# Revit family: 210_CAD O Integral ER 19 VLEXG
name_source: partatom
category: Mechanical Equipment
units: mm (PartAtom-declared; Revit-internal decimal feet)

## family parameters
Always vertical = Yes
Cut with Voids When Loaded = No
Part Type = Breaks Into
Room Calculation Point = No
Round Connector Dimension = Use Diameter
Shared = No
Work Plane-Based = No

## types (1)
- CAD O Integral ER 19 VLEXG
    AA1 = 730 mm
    AA2 = 730 mm
    AA3 = 58 mm  [stored 0.190289 ft]
    AA3__ve = -58 mm  [stored -0.190289 ft]
    AA4 = 788 mm
    BB1 = 408 mm  [stored 1.33858 ft]
    CAT0 = Yes
    D = 355 mm
    HH1 = 1085 mm  [stored 3.55971 ft]
    Manufacturer = VIM
    QmdConnectorList = 221;D;231;D;241;D;251;D
    R = 178 mm  [stored 0.58399 ft]
    SPG = 356 mm  [stored 1.16798 ft]
    SPH = 826 mm  [stored 2.70997 ft]
    SPI1 = 408 mm  [stored 1.33858 ft]
    SPI2 = 408 mm  [stored 1.33858 ft]
    SPN = 1719 mm  [stored 5.63976 ft]
    SPR = 89 mm  [stored 0.291995 ft]
    SPS = 54 mm  [stored 0.177165 ft]
    SS1 = 500 mm  [stored 1.64042 ft]
    SS2 = 860 mm
    W = 500 mm  [stored 1.64042 ft]
    magiPartTypeId = 210
    magiProductCode = CAD O Integral ER 19 VLEXG
    magiProductFamilyId = CAD O Integral ER 19 VLEXG
    magiProductId = CAD O Integral ER 19 VLEXG

note: [stored X ft] marks values corroborated as IEEE doubles in the binary element streams (Revit-internal decimal feet)

## geometry (parser evidence)
native form markers: Sweep x2
no freeform markers — native parametric forms only
